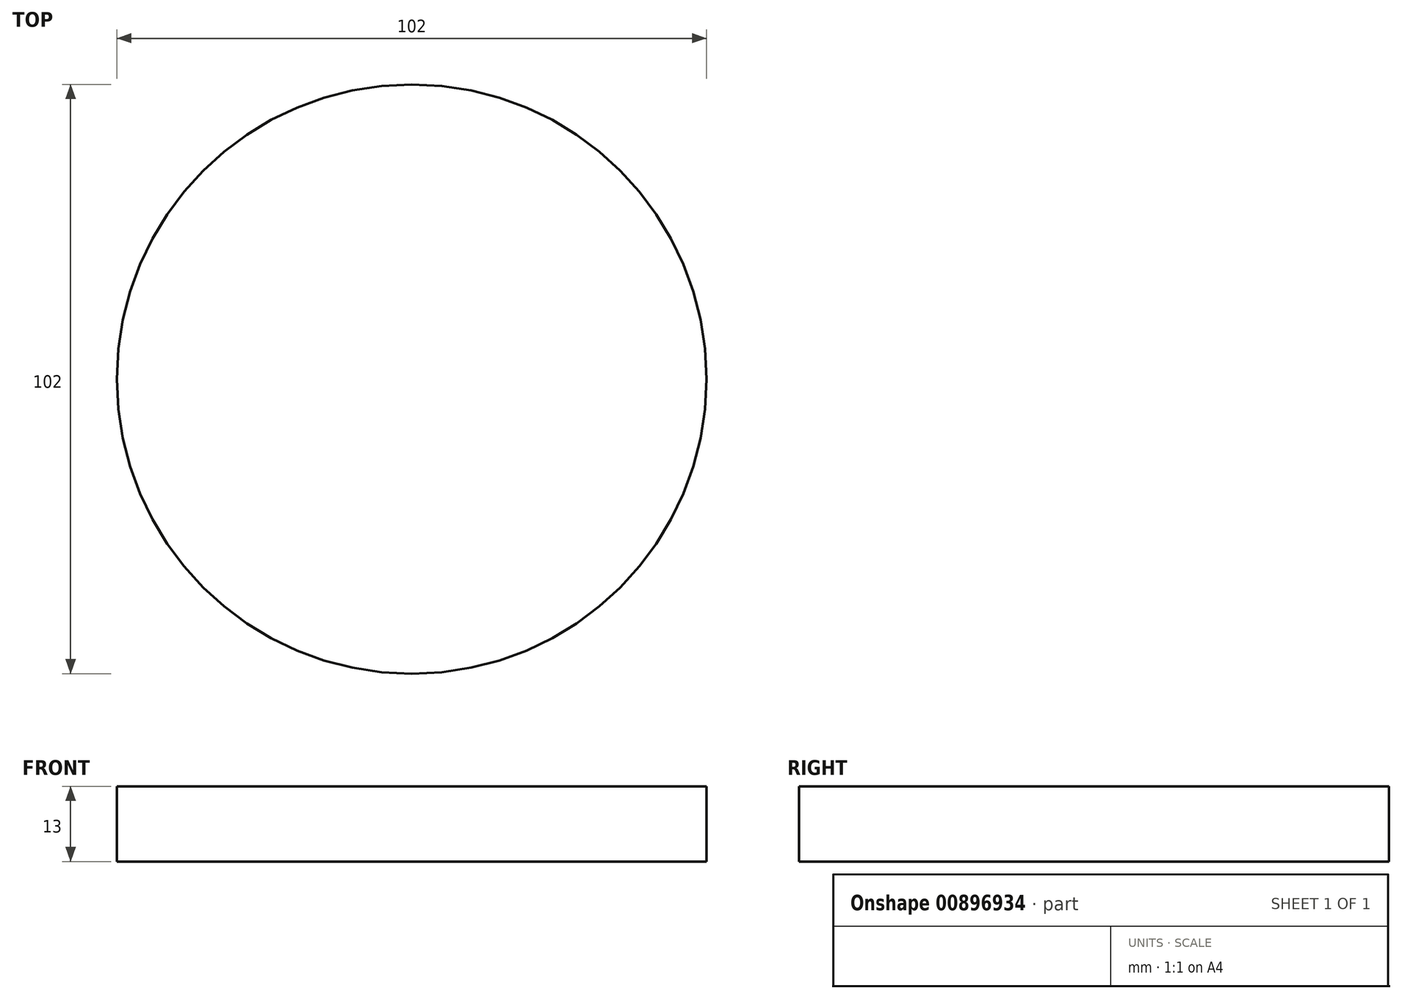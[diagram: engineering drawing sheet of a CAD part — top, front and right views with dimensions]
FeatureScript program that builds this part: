
annotation { "Feature Type Name" : "Feature", "Feature Type Description" : "" }
export const myFeature = defineFeature(function(context is Context, id is Id, definition is map)
    precondition{}
    {
        {
            var Q0;
            Q0=qCreatedBy(makeId("Top.planeOp"),FACE);
            var sketch = newSketch(context, id + "F0", { "sketchPlane" : qUnion([Q0])});
            skCircle(sketch, "E0", {"center": v(0, 0) * mm, "radius": 51 * mm});
            skLineSegment(sketch, "E1", {"start": v(0, -51) * mm, "end": v(0, -53) * mm});
            skArc(sketch, "E2", {"start": v(-51, 0) * mm, "mid": v(0, -53) * mm, "end": v(51, 0) * mm});
            skSolve(sketch);
        }
        {
            var Q0;
            {var subQ0=sQuery(id+"F0.wireOp",EDGE,"E2");var subQ1=sQuery(id+"F0.wireOp",EDGE,"E0");var subQ2=makeQuery(id+"F0.imprint","INTERSECT",VERTEX,{"disambiguationData":[OD(0.0)],"derivedFrom":[subQ1,subQ0]});Q0=makeQuery(id+"F0.imprint","IMPRINT",FACE,{"disambiguationData":[TD([[makeQuery(id+"F0.imprint","IMPRINT",EDGE,{"disambiguationData":[TD([[subQ2,1.0]])],"derivedFrom":subQ1}),1.0]])]});}
            extrude(context, id + "F1", {"entities" : qUnion([Q0]), "depth" : 13 * mm, "offsetDistance" : 25 * mm});
        }
    });
